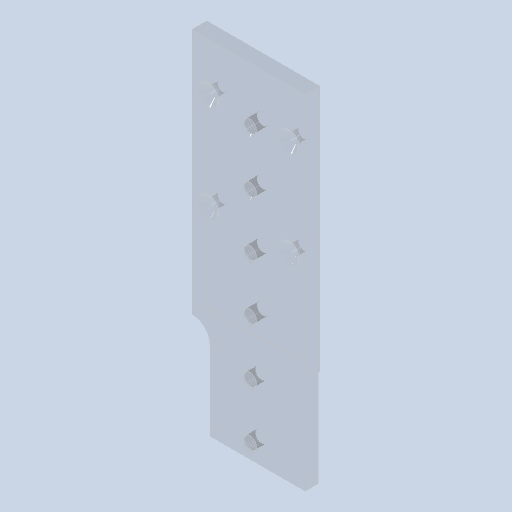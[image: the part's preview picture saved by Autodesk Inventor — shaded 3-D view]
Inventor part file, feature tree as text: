
AUTODESK INVENTOR PART (.ipt)
format: ipt  version: 2022 (Build 260153000, 153)  size: 189,952 bytes
history: native  units: mm
features: thread x6, sketch x2, extrude x2, hole x1, chamfer x1, plane x1, other x1
ambient origin geometry x8: Origin, YZ Plane, XZ Plane, XY Plane, X Axis, Y Axis, Z Axis, Center Point
bodies: Solid1 (feature_tree)
feature tree (14):
  sketch  "Sketch1"  dims[d0=5.5mm d1=76.5mm]
  extrude  "Extrusion1"  Depth=76.5mm
  hole  "Hole1"  [1 undecoded]
  extrude  "Extrusion2"  Depth=4.0mm
  chamfer  "Chamfer1"  Distance=3.8mm
  thread  "Thread1"  [1 undecoded]
  thread  "Thread2"  [1 undecoded]
  thread  "Thread3"  [1 undecoded]
  thread  "Thread4"  [1 undecoded]
  thread  "Thread5"  [1 undecoded]
  thread  "Thread6"  [1 undecoded]
  plane  "Work Plane1"
  sketch  "Sketch2"  dims[d2=35.0mm d3=106.5mm d5=17.5mm d6=3.8mm d7=60.0mm d9=17.0mm d10=10.0mm d12=10.0mm d14=85.0mm d15=4.0mm d16=6.6mm d17=3.2mm d18=20.0mm d20=30.0mm d21=10.0mm d23=10.0mm d25=30.0mm d26=4.5mm d27=0.0mm d28=3.2mm d29=6.0mm d30=6.6mm d31=2.0mm d32=90.0deg d33=8.0mm d34=20.594885mm d35=4.0mm d36=0.0mm d37=0.5mm d38=2.0mm d39=45.0deg d40=4.0mm d41=0.0mm d42=4.0mm d43=0.0mm d44=4.0mm d45=0.0mm d46=3.5mm d47=0.0mm d48=3.5mm d49=0.0mm d50=4.0mm d51=0.0mm d52=90.0deg d53=5.0mm d54=15.0mm]
  other  "Work Axis1"
note: 7 required parameter values undecoded (feature->parameter linkage not recoverable at this tier; creation-order binding heuristic only, values carry confidence <= 0.55)
